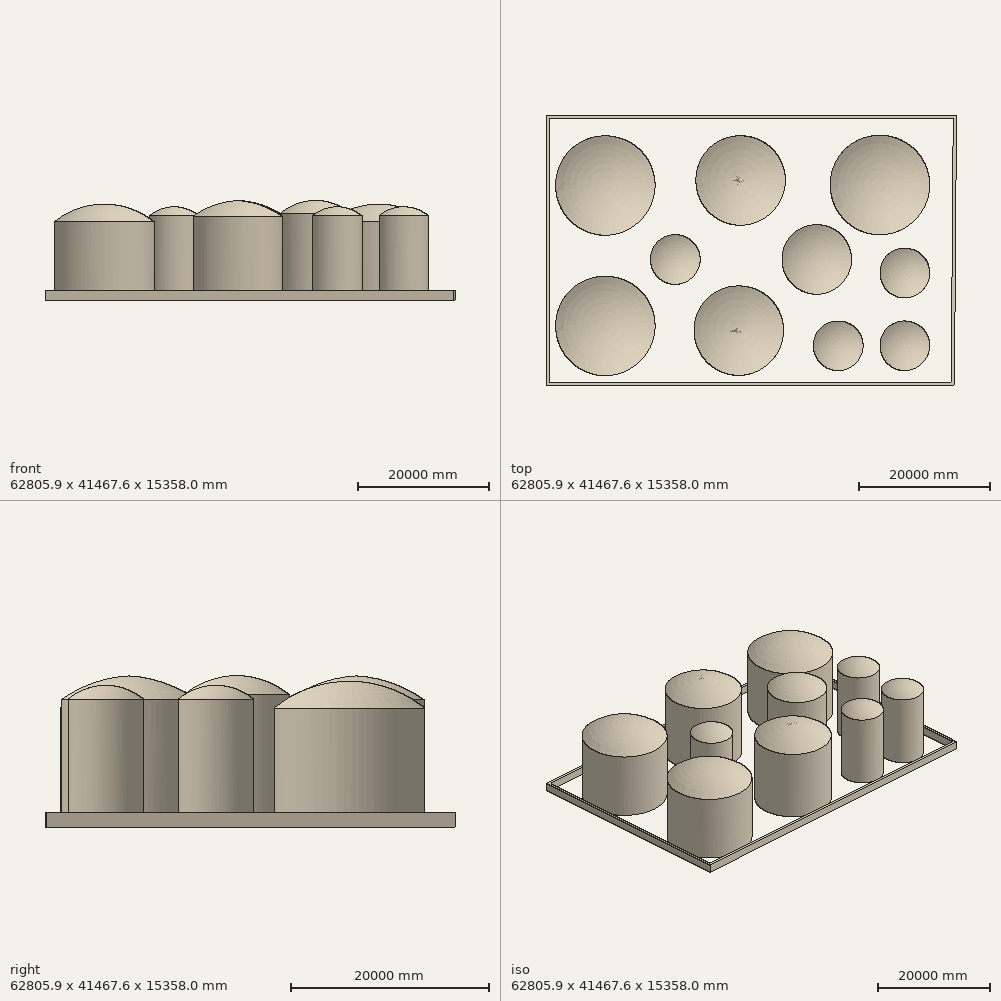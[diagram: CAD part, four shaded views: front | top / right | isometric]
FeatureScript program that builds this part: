
annotation { "Feature Type Name" : "Feature", "Feature Type Description" : "" }
export const myFeature = defineFeature(function(context is Context, id is Id, definition is map)
    precondition{}
    {
        {
            var Q0;
            Q0=qCreatedBy(makeId("Top.planeOp"),FACE);
            var sketch = newSketch(context, id + "F0", { "sketchPlane" : qUnion([Q0])});
            skCircle(sketch, "E0", {"center": v(-23702.7, -8591.04) * mm, "radius": 7620 * mm});
            skCircle(sketch, "E1", {"center": v(-3529.09, -11968.15) * mm, "radius": 6858 * mm});
            skCircle(sketch, "E2", {"center": v(-11745.08, 95.3) * mm, "radius": 3800 * mm});
            skCircle(sketch, "E3", {"center": v(-20898.1, 12736.27) * mm, "radius": 7620 * mm});
            skCircle(sketch, "E4", {"center": v(-255.2, 10798.2) * mm, "radius": 6858 * mm});
            skCircle(sketch, "E5", {"center": v(20818.07, 7322.45) * mm, "radius": 7620 * mm});
            skCircle(sketch, "E6", {"center": v(9737.43, -2722.22) * mm, "radius": 5350 * mm});
            skCircle(sketch, "E7", {"center": v(22839.84, -6549.64) * mm, "radius": 3800 * mm});
            skCircle(sketch, "E8", {"center": v(11264.54, -16270.42) * mm, "radius": 3800 * mm});
            skCircle(sketch, "E9", {"center": v(21386.21, -17593.74) * mm, "radius": 3800 * mm});
            skLineSegment(sketch, "E10", {"start": v(-28432.2, 24599.06) * mm, "end": v(-33837.55, -16505.37) * mm});
            skLineSegment(sketch, "E11", {"start": v(-33837.55, -16505.37) * mm, "end": v(28121.2, -24599.06) * mm});
            skLineSegment(sketch, "E12", {"start": v(28121.2, -24599.06) * mm, "end": v(33837.55, 16410.4) * mm});
            skLineSegment(sketch, "E13", {"start": v(33837.55, 16410.4) * mm, "end": v(-28432.2, 24599.06) * mm});
            skSolve(sketch);
        }
        {
            var Q0;
            Q0=qCreatedBy(makeId("Front.planeOp"),FACE);
            var sketch = newSketch(context, id + "F1", { "sketchPlane" : qUnion([Q0])});
            skLineSegment(sketch, "E14", {"start": v(0, 0) * mm, "end": v(0, 14787.18) * mm, "construction": true});
            skLineSegment(sketch, "E15", {"start": v(0, 0) * mm, "end": v(7620, 0) * mm});
            skLineSegment(sketch, "E16", {"start": v(7620, 0) * mm, "end": v(7620, 12074.18) * mm});
            skArc(sketch, "E17", {"start": v(7620, 12074.18) * mm, "mid": v(4041.34, 14080.44) * mm, "end": v(0, 14787.18) * mm});
            skLineSegment(sketch, "E18", {"start": v(0, 14787.18) * mm, "end": v(0, 0) * mm});
            skSolve(sketch);
        }
        {
            var Q0;
            Q0 = qSketchRegion(id + "F1", true);
            var Q1;
            Q1=sQuery(id+"F1.wireOp",EDGE,"E18");
            revolve(context, id + "F2", {"surfaceOperationType" : NewSurfaceOperationType.NEW, "entities" : qUnion([Q0]), "axis" : qUnion([Q1]), "revolveType" : RevolveType.FULL});
        }
        {
            var Q0;
            Q0=makeQuery(id+"F2.opRevolve","SWEPT_BODY",BODY,{"disambiguationData":[OSD([sQuery(id+"F1.wireOp",EDGE,"E15"),sQuery(id+"F1.wireOp",EDGE,"E16"),sQuery(id+"F1.wireOp",EDGE,"E17"),sQuery(id+"F1.wireOp",EDGE,"E18")])]});
            var Q1;
            Q1=qCreatedBy(makeId("Origin.pointOp"),VERTEX);
            var Q2;
            Q2=sQuery(id+"F0.wireOp",VERTEX,"E5.center");
            transform(context, id + "F3", {"entities" : qUnion([Q0]), "transformType" : TransformType.TRANSLATION_ENTITY, "oppositeDirectionEntity" : false, "transformLine" : qUnion([Q1, Q2]), "makeCopy" : false});
        }
        {
            var Q0;
            Q0=makeQuery(id+"F2.opRevolve","SWEPT_BODY",BODY,{"disambiguationData":[OSD([sQuery(id+"F1.wireOp",EDGE,"E15"),sQuery(id+"F1.wireOp",EDGE,"E16"),sQuery(id+"F1.wireOp",EDGE,"E17"),sQuery(id+"F1.wireOp",EDGE,"E18")])]});
            var Q1;
            Q1=sQuery(id+"F0.wireOp",VERTEX,"E5.center");
            var Q2;
            Q2=sQuery(id+"F0.wireOp",VERTEX,"E3.center");
            transform(context, id + "F4", {"entities" : qUnion([Q0]), "transformType" : TransformType.TRANSLATION_ENTITY, "oppositeDirectionEntity" : false, "transformLine" : qUnion([Q1, Q2]), "makeCopy" : true});
        }
        {
            var Q0;
            Q0=makeQuery(id+"F4.opPattern","COPY",BODY,{"derivedFrom":makeQuery(id+"F2.opRevolve","SWEPT_BODY",BODY,{"disambiguationData":[OSD([sQuery(id+"F1.wireOp",EDGE,"E15"),sQuery(id+"F1.wireOp",EDGE,"E16"),sQuery(id+"F1.wireOp",EDGE,"E17"),sQuery(id+"F1.wireOp",EDGE,"E18")])]}),"instanceName":"1"});
            var Q1;
            Q1=sQuery(id+"F0.wireOp",VERTEX,"E3.center");
            var Q2;
            Q2=sQuery(id+"F0.wireOp",VERTEX,"E0.center");
            transform(context, id + "F5", {"entities" : qUnion([Q0]), "transformType" : TransformType.TRANSLATION_ENTITY, "oppositeDirectionEntity" : false, "transformLine" : qUnion([Q1, Q2]), "makeCopy" : true});
        }
        {
            var Q0;
            Q0=qCreatedBy(makeId("Front.planeOp"),FACE);
            var sketch = newSketch(context, id + "F6", { "sketchPlane" : qUnion([Q0])});
            skLineSegment(sketch, "E19", {"start": v(0, 0) * mm, "end": v(0, 15332) * mm});
            skLineSegment(sketch, "E20", {"start": v(0, 0) * mm, "end": v(6858, 0) * mm});
            skLineSegment(sketch, "E21", {"start": v(6858, 0) * mm, "end": v(6858, 12888) * mm});
            skArc(sketch, "E22", {"start": v(6858, 12888) * mm, "mid": v(3603.82, 14600.56) * mm, "end": v(0, 15332) * mm});
            skSolve(sketch);
        }
        {
            var Q0;
            Q0 = qSketchRegion(id + "F6", true);
            var Q1;
            Q1=sQuery(id+"F6.wireOp",EDGE,"E19");
            revolve(context, id + "F7", {"surfaceOperationType" : NewSurfaceOperationType.NEW, "entities" : qUnion([Q0]), "axis" : qUnion([Q1]), "revolveType" : RevolveType.FULL});
        }
        {
            var Q0;
            Q0=makeQuery(id+"F7.opRevolve","SWEPT_BODY",BODY,{"disambiguationData":[OSD([sQuery(id+"F6.wireOp",EDGE,"E19"),sQuery(id+"F6.wireOp",EDGE,"E20"),sQuery(id+"F6.wireOp",EDGE,"E21"),sQuery(id+"F6.wireOp",EDGE,"E22")])]});
            var Q1;
            Q1=qCreatedBy(makeId("Origin.pointOp"),VERTEX);
            var Q2;
            Q2=sQuery(id+"F0.wireOp",VERTEX,"E4.center");
            transform(context, id + "F8", {"entities" : qUnion([Q0]), "transformType" : TransformType.TRANSLATION_ENTITY, "oppositeDirectionEntity" : false, "transformLine" : qUnion([Q1, Q2]), "makeCopy" : false});
        }
        {
            var Q0;
            Q0=makeQuery(id+"F7.opRevolve","SWEPT_BODY",BODY,{"disambiguationData":[OSD([sQuery(id+"F6.wireOp",EDGE,"E19"),sQuery(id+"F6.wireOp",EDGE,"E20"),sQuery(id+"F6.wireOp",EDGE,"E21"),sQuery(id+"F6.wireOp",EDGE,"E22")])]});
            var Q1;
            Q1=sQuery(id+"F0.wireOp",VERTEX,"E4.center");
            var Q2;
            Q2=sQuery(id+"F0.wireOp",VERTEX,"E1.center");
            transform(context, id + "F9", {"entities" : qUnion([Q0]), "transformType" : TransformType.TRANSLATION_ENTITY, "oppositeDirectionEntity" : false, "transformLine" : qUnion([Q1, Q2]), "makeCopy" : true});
        }
        {
            var Q0;
            Q0=qCreatedBy(makeId("Front.planeOp"),FACE);
            var sketch = newSketch(context, id + "F10", { "sketchPlane" : qUnion([Q0])});
            skLineSegment(sketch, "E23", {"start": v(0, 0) * mm, "end": v(3810, 0) * mm});
            skLineSegment(sketch, "E24", {"start": v(3810, 0) * mm, "end": v(3810, 12964) * mm});
            skLineSegment(sketch, "E25", {"start": v(0, 0) * mm, "end": v(0, 14384) * mm});
            skArc(sketch, "E26", {"start": v(3810, 12964) * mm, "mid": v(2026.7, 14000.5) * mm, "end": v(0, 14384) * mm});
            skSolve(sketch);
        }
        {
            var Q0;
            Q0 = qSketchRegion(id + "F10", true);
            var Q1;
            Q1=sQuery(id+"F10.wireOp",EDGE,"E25");
            revolve(context, id + "F11", {"surfaceOperationType" : NewSurfaceOperationType.NEW, "entities" : qUnion([Q0]), "axis" : qUnion([Q1]), "revolveType" : RevolveType.FULL});
        }
        {
            var Q0;
            Q0=makeQuery(id+"F11.opRevolve","SWEPT_BODY",BODY,{"disambiguationData":[OSD([sQuery(id+"F10.wireOp",EDGE,"E23"),sQuery(id+"F10.wireOp",EDGE,"E24"),sQuery(id+"F10.wireOp",EDGE,"E25"),sQuery(id+"F10.wireOp",EDGE,"E26")])]});
            var Q1;
            Q1=qCreatedBy(makeId("Origin.pointOp"),VERTEX);
            var Q2;
            Q2=sQuery(id+"F0.wireOp",VERTEX,"E2.center");
            transform(context, id + "F12", {"entities" : qUnion([Q0]), "transformType" : TransformType.TRANSLATION_ENTITY, "oppositeDirectionEntity" : false, "transformLine" : qUnion([Q1, Q2]), "makeCopy" : false});
        }
        {
            var Q0;
            Q0=makeQuery(id+"F11.opRevolve","SWEPT_BODY",BODY,{"disambiguationData":[OSD([sQuery(id+"F10.wireOp",EDGE,"E23"),sQuery(id+"F10.wireOp",EDGE,"E24"),sQuery(id+"F10.wireOp",EDGE,"E25"),sQuery(id+"F10.wireOp",EDGE,"E26")])]});
            var Q1;
            Q1=sQuery(id+"F0.wireOp",VERTEX,"E2.center");
            var Q2;
            Q2=sQuery(id+"F0.wireOp",VERTEX,"E7.center");
            transform(context, id + "F13", {"entities" : qUnion([Q0]), "transformType" : TransformType.TRANSLATION_ENTITY, "oppositeDirectionEntity" : false, "transformLine" : qUnion([Q1, Q2]), "makeCopy" : true});
        }
        {
            var Q0;
            Q0=makeQuery(id+"F13.opPattern","COPY",BODY,{"derivedFrom":makeQuery(id+"F11.opRevolve","SWEPT_BODY",BODY,{"disambiguationData":[OSD([sQuery(id+"F10.wireOp",EDGE,"E23"),sQuery(id+"F10.wireOp",EDGE,"E24"),sQuery(id+"F10.wireOp",EDGE,"E25"),sQuery(id+"F10.wireOp",EDGE,"E26")])]}),"instanceName":"1"});
            var Q1;
            Q1=sQuery(id+"F0.wireOp",VERTEX,"E7.center");
            var Q2;
            Q2=sQuery(id+"F0.wireOp",VERTEX,"E8.center");
            transform(context, id + "F14", {"entities" : qUnion([Q0]), "transformType" : TransformType.TRANSLATION_ENTITY, "oppositeDirectionEntity" : false, "transformLine" : qUnion([Q1, Q2]), "makeCopy" : true});
        }
        {
            var Q0;
            Q0=makeQuery(id+"F14.opPattern","COPY",BODY,{"derivedFrom":makeQuery(id+"F13.opPattern","COPY",BODY,{"derivedFrom":makeQuery(id+"F11.opRevolve","SWEPT_BODY",BODY,{"disambiguationData":[OSD([sQuery(id+"F10.wireOp",EDGE,"E23"),sQuery(id+"F10.wireOp",EDGE,"E24"),sQuery(id+"F10.wireOp",EDGE,"E25"),sQuery(id+"F10.wireOp",EDGE,"E26")])]}),"instanceName":"1"}),"instanceName":"1"});
            var Q1;
            Q1=sQuery(id+"F0.wireOp",VERTEX,"E8.center");
            var Q2;
            Q2=sQuery(id+"F0.wireOp",VERTEX,"E9.center");
            transform(context, id + "F15", {"entities" : qUnion([Q0]), "transformType" : TransformType.TRANSLATION_ENTITY, "oppositeDirectionEntity" : false, "transformLine" : qUnion([Q1, Q2]), "makeCopy" : true});
        }
        {
            var Q0;
            Q0=qCreatedBy(makeId("Front.planeOp"),FACE);
            var sketch = newSketch(context, id + "F16", { "sketchPlane" : qUnion([Q0])});
            skLineSegment(sketch, "E27", {"start": v(0, 15358) * mm, "end": v(0, 0) * mm});
            skLineSegment(sketch, "E28", {"start": v(0, 0) * mm, "end": v(5334, 0) * mm});
            skLineSegment(sketch, "E29", {"start": v(5334, 0) * mm, "end": v(5334, 13411) * mm});
            skArc(sketch, "E30", {"start": v(5334, 13411) * mm, "mid": v(2833.41, 14840.4) * mm, "end": v(0, 15358) * mm});
            skSolve(sketch);
        }
        {
            var Q0;
            Q0 = qSketchRegion(id + "F16", true);
            var Q1;
            Q1=sQuery(id+"F16.wireOp",EDGE,"E27");
            revolve(context, id + "F17", {"surfaceOperationType" : NewSurfaceOperationType.NEW, "entities" : qUnion([Q0]), "axis" : qUnion([Q1]), "revolveType" : RevolveType.FULL});
        }
        {
            var Q0;
            Q0=makeQuery(id+"F17.opRevolve","SWEPT_BODY",BODY,{"disambiguationData":[OSD([sQuery(id+"F16.wireOp",EDGE,"E27"),sQuery(id+"F16.wireOp",EDGE,"E28"),sQuery(id+"F16.wireOp",EDGE,"E29"),sQuery(id+"F16.wireOp",EDGE,"E30")])]});
            var Q1;
            Q1=qCreatedBy(makeId("Origin.pointOp"),VERTEX);
            var Q2;
            Q2=sQuery(id+"F0.wireOp",VERTEX,"E6.center");
            transform(context, id + "F18", {"entities" : qUnion([Q0]), "transformType" : TransformType.TRANSLATION_ENTITY, "oppositeDirectionEntity" : false, "transformLine" : qUnion([Q1, Q2]), "makeCopy" : false});
        }
        {
            var Q0;
            Q0=qCreatedBy(makeId("Top.planeOp"),FACE);
            var sketch = newSketch(context, id + "F19", { "sketchPlane" : qUnion([Q0])});
            skLineSegment(sketch, "E31.0", {"start": v(33837.55, 16410.4) * mm, "end": v(-28432.2, 24599.06) * mm});
            skLineSegment(sketch, "E31.1", {"start": v(-28432.2, 24599.06) * mm, "end": v(-33837.55, -16505.37) * mm});
            skLineSegment(sketch, "E31.2", {"start": v(-33837.55, -16505.37) * mm, "end": v(28121.2, -24599.06) * mm});
            skLineSegment(sketch, "E31.3", {"start": v(28121.2, -24599.06) * mm, "end": v(33837.55, 16410.4) * mm});
            skLineSegment(sketch, "E32.0", {"start": v(-28001.66, 24038.14) * mm, "end": v(-33276.57, -16074.4) * mm});
            skLineSegment(sketch, "E32.1", {"start": v(33272.77, 15980.37) * mm, "end": v(-28001.66, 24038.14) * mm});
            skLineSegment(sketch, "E32.2", {"start": v(27694.42, -24039.06) * mm, "end": v(33272.77, 15980.37) * mm});
            skLineSegment(sketch, "E32.3", {"start": v(-33276.57, -16074.4) * mm, "end": v(27694.42, -24039.06) * mm});
            skSolve(sketch);
        }
        {
            var Q0;
            Q0 = qSketchRegion(id + "F19", true);
            extrude(context, id + "F20", {"entities" : qUnion([Q0]), "depth" : 1500 * mm, "offsetDistance" : 25 * mm});
        }
        {
            var Q0;
            Q0=qCreatedBy(makeId("Front.planeOp"),FACE);
            var sketch = newSketch(context, id + "F21", { "sketchPlane" : qUnion([Q0])});
            skLineSegment(sketch, "E33", {"start": v(0, 0) * mm, "end": v(0, 26049.16) * mm, "construction": true});
            skSolve(sketch);
        }
        {
            var Q0;
            Q0=makeQuery(id+"F20.opExtrude","SWEPT_BODY",BODY,{"disambiguationData":[OSD([sQuery(id+"F19.wireOp",EDGE,"E31.0"),sQuery(id+"F19.wireOp",EDGE,"E31.1"),sQuery(id+"F19.wireOp",EDGE,"E31.2"),sQuery(id+"F19.wireOp",EDGE,"E31.3"),sQuery(id+"F19.wireOp",EDGE,"E32.0"),sQuery(id+"F19.wireOp",EDGE,"E32.1"),sQuery(id+"F19.wireOp",EDGE,"E32.2"),sQuery(id+"F19.wireOp",EDGE,"E32.3")])]});
            var Q1;
            Q1=makeQuery(id+"F17.opRevolve","SWEPT_BODY",BODY,{"disambiguationData":[OSD([sQuery(id+"F16.wireOp",EDGE,"E27"),sQuery(id+"F16.wireOp",EDGE,"E28"),sQuery(id+"F16.wireOp",EDGE,"E29"),sQuery(id+"F16.wireOp",EDGE,"E30")])]});
            var Q2;
            Q2=makeQuery(id+"F15.opPattern","COPY",BODY,{"derivedFrom":makeQuery(id+"F14.opPattern","COPY",BODY,{"derivedFrom":makeQuery(id+"F13.opPattern","COPY",BODY,{"derivedFrom":makeQuery(id+"F11.opRevolve","SWEPT_BODY",BODY,{"disambiguationData":[OSD([sQuery(id+"F10.wireOp",EDGE,"E23"),sQuery(id+"F10.wireOp",EDGE,"E24"),sQuery(id+"F10.wireOp",EDGE,"E25"),sQuery(id+"F10.wireOp",EDGE,"E26")])]}),"instanceName":"1"}),"instanceName":"1"}),"instanceName":"1"});
            var Q3;
            Q3=makeQuery(id+"F14.opPattern","COPY",BODY,{"derivedFrom":makeQuery(id+"F13.opPattern","COPY",BODY,{"derivedFrom":makeQuery(id+"F11.opRevolve","SWEPT_BODY",BODY,{"disambiguationData":[OSD([sQuery(id+"F10.wireOp",EDGE,"E23"),sQuery(id+"F10.wireOp",EDGE,"E24"),sQuery(id+"F10.wireOp",EDGE,"E25"),sQuery(id+"F10.wireOp",EDGE,"E26")])]}),"instanceName":"1"}),"instanceName":"1"});
            var Q4;
            Q4=makeQuery(id+"F13.opPattern","COPY",BODY,{"derivedFrom":makeQuery(id+"F11.opRevolve","SWEPT_BODY",BODY,{"disambiguationData":[OSD([sQuery(id+"F10.wireOp",EDGE,"E23"),sQuery(id+"F10.wireOp",EDGE,"E24"),sQuery(id+"F10.wireOp",EDGE,"E25"),sQuery(id+"F10.wireOp",EDGE,"E26")])]}),"instanceName":"1"});
            var Q5;
            Q5=makeQuery(id+"F11.opRevolve","SWEPT_BODY",BODY,{"disambiguationData":[OSD([sQuery(id+"F10.wireOp",EDGE,"E23"),sQuery(id+"F10.wireOp",EDGE,"E24"),sQuery(id+"F10.wireOp",EDGE,"E25"),sQuery(id+"F10.wireOp",EDGE,"E26")])]});
            var Q6;
            Q6=makeQuery(id+"F9.opPattern","COPY",BODY,{"derivedFrom":makeQuery(id+"F7.opRevolve","SWEPT_BODY",BODY,{"disambiguationData":[OSD([sQuery(id+"F6.wireOp",EDGE,"E19"),sQuery(id+"F6.wireOp",EDGE,"E20"),sQuery(id+"F6.wireOp",EDGE,"E21"),sQuery(id+"F6.wireOp",EDGE,"E22")])]}),"instanceName":"1"});
            var Q7;
            Q7=makeQuery(id+"F2.opRevolve","SWEPT_BODY",BODY,{"disambiguationData":[OSD([sQuery(id+"F1.wireOp",EDGE,"E15"),sQuery(id+"F1.wireOp",EDGE,"E16"),sQuery(id+"F1.wireOp",EDGE,"E17"),sQuery(id+"F1.wireOp",EDGE,"E18")])]});
            var Q8;
            Q8=makeQuery(id+"F5.opPattern","COPY",BODY,{"derivedFrom":makeQuery(id+"F4.opPattern","COPY",BODY,{"derivedFrom":makeQuery(id+"F2.opRevolve","SWEPT_BODY",BODY,{"disambiguationData":[OSD([sQuery(id+"F1.wireOp",EDGE,"E15"),sQuery(id+"F1.wireOp",EDGE,"E16"),sQuery(id+"F1.wireOp",EDGE,"E17"),sQuery(id+"F1.wireOp",EDGE,"E18")])]}),"instanceName":"1"}),"instanceName":"1"});
            var Q9;
            Q9=makeQuery(id+"F4.opPattern","COPY",BODY,{"derivedFrom":makeQuery(id+"F2.opRevolve","SWEPT_BODY",BODY,{"disambiguationData":[OSD([sQuery(id+"F1.wireOp",EDGE,"E15"),sQuery(id+"F1.wireOp",EDGE,"E16"),sQuery(id+"F1.wireOp",EDGE,"E17"),sQuery(id+"F1.wireOp",EDGE,"E18")])]}),"instanceName":"1"});
            var Q10;
            Q10=makeQuery(id+"F7.opRevolve","SWEPT_BODY",BODY,{"disambiguationData":[OSD([sQuery(id+"F6.wireOp",EDGE,"E19"),sQuery(id+"F6.wireOp",EDGE,"E20"),sQuery(id+"F6.wireOp",EDGE,"E21"),sQuery(id+"F6.wireOp",EDGE,"E22")])]});
            var Q11;
            Q11=sQuery(id+"F21.wireOp",EDGE,"E33");
            transform(context, id + "F22", {"entities" : qUnion([Q0, Q1, Q2, Q3, Q4, Q5, Q6, Q7, Q8, Q9, Q10]), "transformType" : TransformType.ROTATION, "transformAxis" : qUnion([Q11]), "angle" : 7.5 * degree, "makeCopy" : false});
        }
    });
